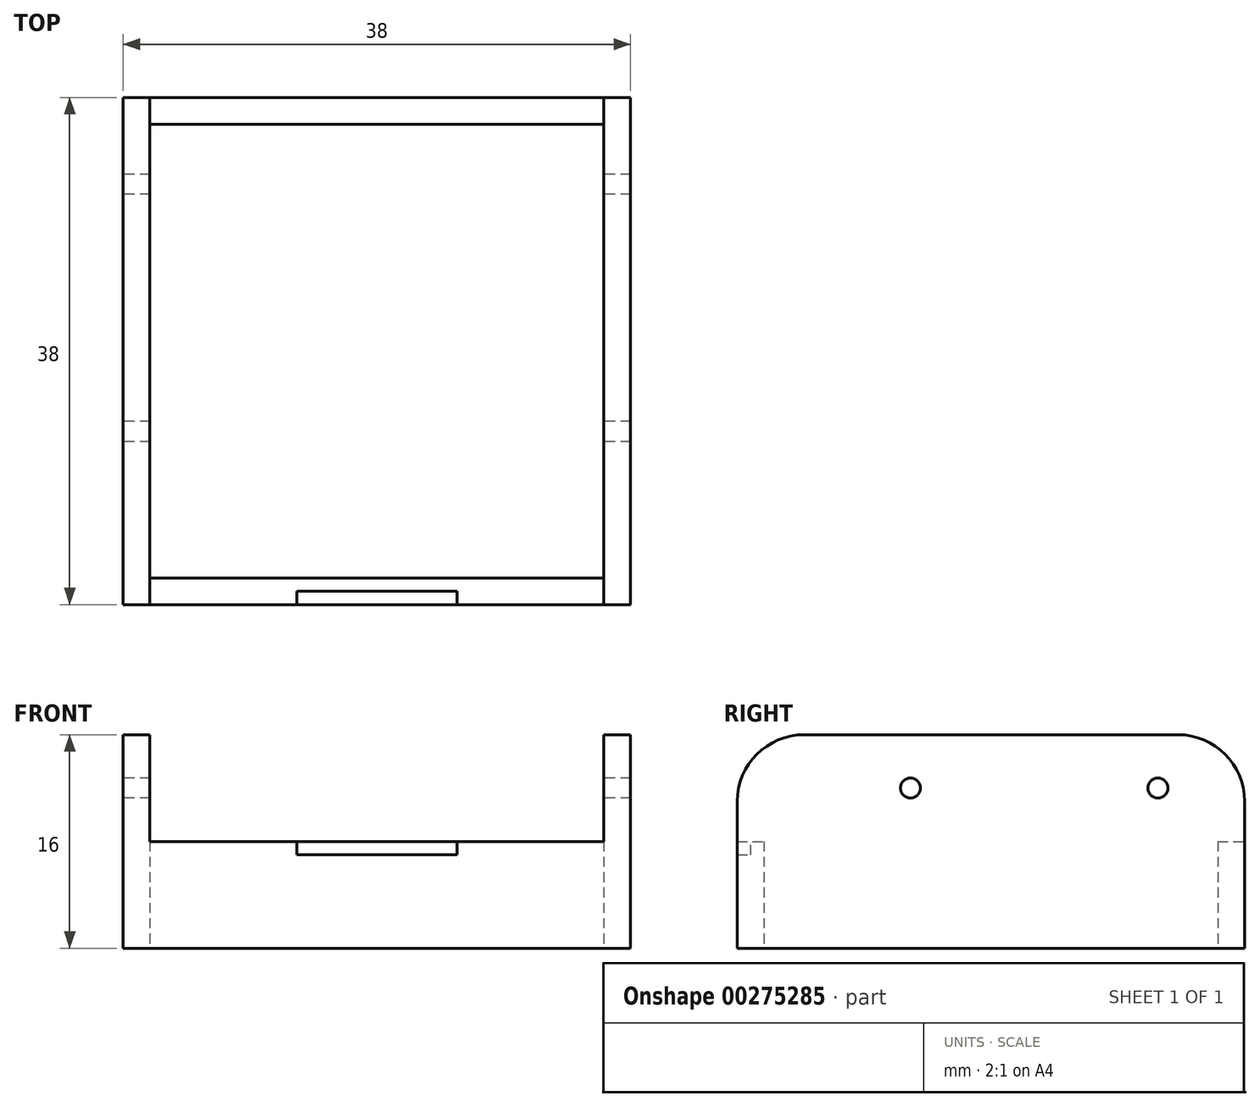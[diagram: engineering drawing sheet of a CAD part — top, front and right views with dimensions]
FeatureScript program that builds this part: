
annotation { "Feature Type Name" : "Feature", "Feature Type Description" : "" }
export const myFeature = defineFeature(function(context is Context, id is Id, definition is map)
    precondition{}
    {
        {
            var Q0;
            Q0=qCreatedBy(makeId("Top.planeOp"),FACE);
            var sketch = newSketch(context, id + "F0", { "sketchPlane" : qUnion([Q0])});
            skLineSegment(sketch, "E0.bottom", {"start": v(0, 0) * mm, "end": v(38, 0) * mm});
            skLineSegment(sketch, "E0.top", {"start": v(0, 38) * mm, "end": v(38, 38) * mm});
            skLineSegment(sketch, "E0.left", {"start": v(0, 0) * mm, "end": v(0, 38) * mm});
            skLineSegment(sketch, "E0.right", {"start": v(38, 0) * mm, "end": v(38, 38) * mm});
            skLineSegment(sketch, "E1.bottom", {"start": v(2, 36) * mm, "end": v(36, 36) * mm});
            skLineSegment(sketch, "E1.top", {"start": v(2, 2) * mm, "end": v(36, 2) * mm});
            skLineSegment(sketch, "E1.left", {"start": v(2, 36) * mm, "end": v(2, 2) * mm});
            skLineSegment(sketch, "E1.right", {"start": v(36, 36) * mm, "end": v(36, 2) * mm});
            skSolve(sketch);
        }
        {
            var Q0;
            Q0=makeQuery(id+"F0.imprint","IMPRINT",FACE,{"disambiguationData":[TD([[makeQuery(id+"F0.imprint","IMPRINT",EDGE,{"derivedFrom":sQuery(id+"F0.wireOp",EDGE,"E0.bottom")}),1.0]])]});
            extrude(context, id + "F1", {"entities" : qUnion([Q0]), "depth" : 8 * mm});
        }
        {
            var Q0;
            Q0=makeQuery(id+"F1.opExtrude","CAP_FACE",FACE,{"disambiguationData":[OSD([sQuery(id+"F0.wireOp",EDGE,"E0.bottom"),sQuery(id+"F0.wireOp",EDGE,"E0.top"),sQuery(id+"F0.wireOp",EDGE,"E0.left"),sQuery(id+"F0.wireOp",EDGE,"E0.right"),sQuery(id+"F0.wireOp",EDGE,"E1.bottom"),sQuery(id+"F0.wireOp",EDGE,"E1.top"),sQuery(id+"F0.wireOp",EDGE,"E1.left"),sQuery(id+"F0.wireOp",EDGE,"E1.right")])],"isStart":false});
            var sketch = newSketch(context, id + "F2", { "sketchPlane" : qUnion([Q0])});
            skLineSegment(sketch, "E2.0", {"start": v(0, 0) * mm, "end": v(38, 0) * mm, "construction": true});
            skLineSegment(sketch, "E3.bottom", {"start": v(19, 0) * mm, "end": v(25, 0) * mm});
            skLineSegment(sketch, "E3.top", {"start": v(19, 1) * mm, "end": v(25, 1) * mm});
            skLineSegment(sketch, "E3.left", {"start": v(19, 0) * mm, "end": v(19, 1) * mm, "construction": true});
            skLineSegment(sketch, "E3.right", {"start": v(25, 0) * mm, "end": v(25, 1) * mm});
            skLineSegment(sketch, "E4.MirrorCS", {"start": v(13, 0) * mm, "end": v(13, 1) * mm});
            skLineSegment(sketch, "E5.MirrorCS", {"start": v(19, 1) * mm, "end": v(13, 1) * mm});
            skLineSegment(sketch, "E6.MirrorCS", {"start": v(19, 0) * mm, "end": v(13, 0) * mm});
            skSolve(sketch);
        }
        {
            var Q0;
            Q0 = qSketchRegion(id + "F2", true);
            extrude(context, id + "F3", {"entities" : qUnion([Q0]), "operationType" : NewBodyOperationType.REMOVE, "oppositeDirection" : true, "depth" : 1 * mm});
        }
        {
            var Q0;
            Q0=makeQuery(id+"F1.opExtrude","CAP_FACE",FACE,{"disambiguationData":[OSD([sQuery(id+"F0.wireOp",EDGE,"E0.bottom"),sQuery(id+"F0.wireOp",EDGE,"E0.top"),sQuery(id+"F0.wireOp",EDGE,"E0.left"),sQuery(id+"F0.wireOp",EDGE,"E0.right"),sQuery(id+"F0.wireOp",EDGE,"E1.bottom"),sQuery(id+"F0.wireOp",EDGE,"E1.top"),sQuery(id+"F0.wireOp",EDGE,"E1.left"),sQuery(id+"F0.wireOp",EDGE,"E1.right")])],"isStart":false});
            var sketch = newSketch(context, id + "F4", { "sketchPlane" : qUnion([Q0])});
            skLineSegment(sketch, "E7.0", {"start": v(0, 0) * mm, "end": v(0, 38) * mm});
            skLineSegment(sketch, "E8.0", {"start": v(2, 36) * mm, "end": v(2, 2) * mm});
            skLineSegment(sketch, "E9.0", {"start": v(36, 36) * mm, "end": v(36, 2) * mm});
            skLineSegment(sketch, "E10.0", {"start": v(38, 0) * mm, "end": v(38, 38) * mm});
            skPoint(sketch, "E11", {"position": v(2, 38) * mm});
            skLineSegment(sketch, "E12", {"start": v(0, 38) * mm, "end": v(2, 38) * mm});
            skLineSegment(sketch, "E13", {"start": v(2, 38) * mm, "end": v(2, 36) * mm});
            skLineSegment(sketch, "E14", {"start": v(36, 36) * mm, "end": v(36, 38) * mm});
            skLineSegment(sketch, "E15", {"start": v(0, 0) * mm, "end": v(2, 0) * mm});
            skLineSegment(sketch, "E16", {"start": v(2, 0) * mm, "end": v(2, 2) * mm});
            skLineSegment(sketch, "E17", {"start": v(36, 2) * mm, "end": v(36, 0) * mm});
            skLineSegment(sketch, "E18", {"start": v(36, 0) * mm, "end": v(38, 0) * mm});
            skSolve(sketch);
        }
        {
            var Q0;
            Q0=makeQuery(id+"F4.imprint","IMPRINT",FACE,{"disambiguationData":[TD([[makeQuery(id+"F4.imprint","IMPRINT",EDGE,{"derivedFrom":sQuery(id+"F4.wireOp",EDGE,"E7.0")}),-1.0]])]});
            var Q1;
            Q1=makeQuery(id+"F4.imprint","IMPRINT",FACE,{"disambiguationData":[TD([[makeQuery(id+"F4.imprint","IMPRINT",EDGE,{"derivedFrom":sQuery(id+"F4.wireOp",EDGE,"E9.0")}),1.0]])]});
            extrude(context, id + "F5", {"entities" : qUnion([Q0, Q1]), "operationType" : NewBodyOperationType.ADD, "depth" : 8 * mm});
        }
        {
            var Q0;
            Q0=makeQuery(id+"F5.boolean.opBoolean","MERGE",FACE,{"derivedFrom":[makeQuery(id+"F1.opExtrude","SWEPT_FACE",FACE,{"disambiguationData":[OSD([sQuery(id+"F0.wireOp",EDGE,"E1.right")])]}),makeQuery(id+"F5.opExtrude","SWEPT_FACE",FACE,{"disambiguationData":[OSD([sQuery(id+"F4.wireOp",EDGE,"E9.0"),sQuery(id+"F4.wireOp",EDGE,"E14"),sQuery(id+"F4.wireOp",EDGE,"E17")])]})]});
            var sketch = newSketch(context, id + "F6", { "sketchPlane" : qUnion([Q0])});
            skPoint(sketch, "E19.0", {"position": v(-38, 12) * mm});
            skPoint(sketch, "E20.0", {"position": v(0, 12) * mm});
            skLineSegment(sketch, "E21", {"start": v(-38, 12) * mm, "end": v(0, 12) * mm, "construction": true});
            skPoint(sketch, "E22", {"position": v(-31.5, 12) * mm});
            skPoint(sketch, "E23", {"position": v(-12.97, 12) * mm});
            skCircle(sketch, "E24", {"center": v(-31.5, 12) * mm, "radius": 0.75 * mm});
            skCircle(sketch, "E25", {"center": v(-12.97, 12) * mm, "radius": 0.75 * mm});
            skLineSegment(sketch, "E26", {"start": v(-38, 8) * mm, "end": v(-38, 11) * mm, "construction": true});
            skLineSegment(sketch, "E27.bottom", {"start": v(-38, 11) * mm, "end": v(-36, 11) * mm});
            skLineSegment(sketch, "E27.top", {"start": v(-38, 16) * mm, "end": v(-36, 16) * mm});
            skLineSegment(sketch, "E27.left", {"start": v(-38, 11) * mm, "end": v(-38, 16) * mm});
            skLineSegment(sketch, "E27.right", {"start": v(-36, 11) * mm, "end": v(-36, 16) * mm});
            skSolve(sketch);
        }
        {
            var Q0;
            Q0=makeQuery(id+"F6.imprint","IMPRINT",FACE,{"disambiguationData":[TD([[makeQuery(id+"F6.imprint","IMPRINT",EDGE,{"derivedFrom":sQuery(id+"F6.wireOp",EDGE,"E24")}),1.0]])]});
            var Q1;
            Q1=makeQuery(id+"F6.imprint","IMPRINT",FACE,{"disambiguationData":[TD([[makeQuery(id+"F6.imprint","IMPRINT",EDGE,{"derivedFrom":sQuery(id+"F6.wireOp",EDGE,"E25")}),1.0]])]});
            extrude(context, id + "F7", {"entities" : qUnion([Q0, Q1]), "operationType" : NewBodyOperationType.REMOVE, "oppositeDirection" : true, "depth" : 50.7 * mm, "hasSecondDirection" : true, "secondDirectionOppositeDirection" : false, "secondDirectionDepth" : 53.4 * mm});
        }
        {
            var Q0;
            Q0=makeQuery(id+"F5.opExtrude","CAP_EDGE",EDGE,{"disambiguationData":[OSD([sQuery(id+"F4.wireOp",EDGE,"E15")])],"isStart":false});
            var Q1;
            Q1=makeQuery(id+"F5.opExtrude","CAP_EDGE",EDGE,{"disambiguationData":[OSD([sQuery(id+"F4.wireOp",EDGE,"E18")])],"isStart":false});
            var Q2;
            Q2=makeQuery(id+"F9zujQFLE5AzgeU_1.boolean.opBoolean","MERGE",EDGE,{"derivedFrom":[makeQuery(id+"F5.opExtrude","CAP_EDGE",EDGE,{"disambiguationData":[OSD([sQuery(id+"F4.wireOp",EDGE,"E12")])],"isStart":false}),makeQuery(id+"F5.opExtrude","CAP_EDGE",EDGE,{"disambiguationData":[OSD([sQuery(id+"F0.wireOp",EDGE,"E0.top")])],"isStart":false}),makeQuery(id+"F9zujQFLE5AzgeU_1.opExtrude","SWEPT_EDGE",EDGE,{"disambiguationData":[OSD([sQuery(id+"F6.wireOp",EDGE,"E27.top"),sQuery(id+"F6.wireOp",EDGE,"E27.left")])]})]});
            fillet(context, id + "F8", {"entities" : qUnion([Q0, Q1, Q2]), "radius" : 5 * mm, "tangentPropagation" : true, "allowEdgeOverflow" : false});
        }
    });
